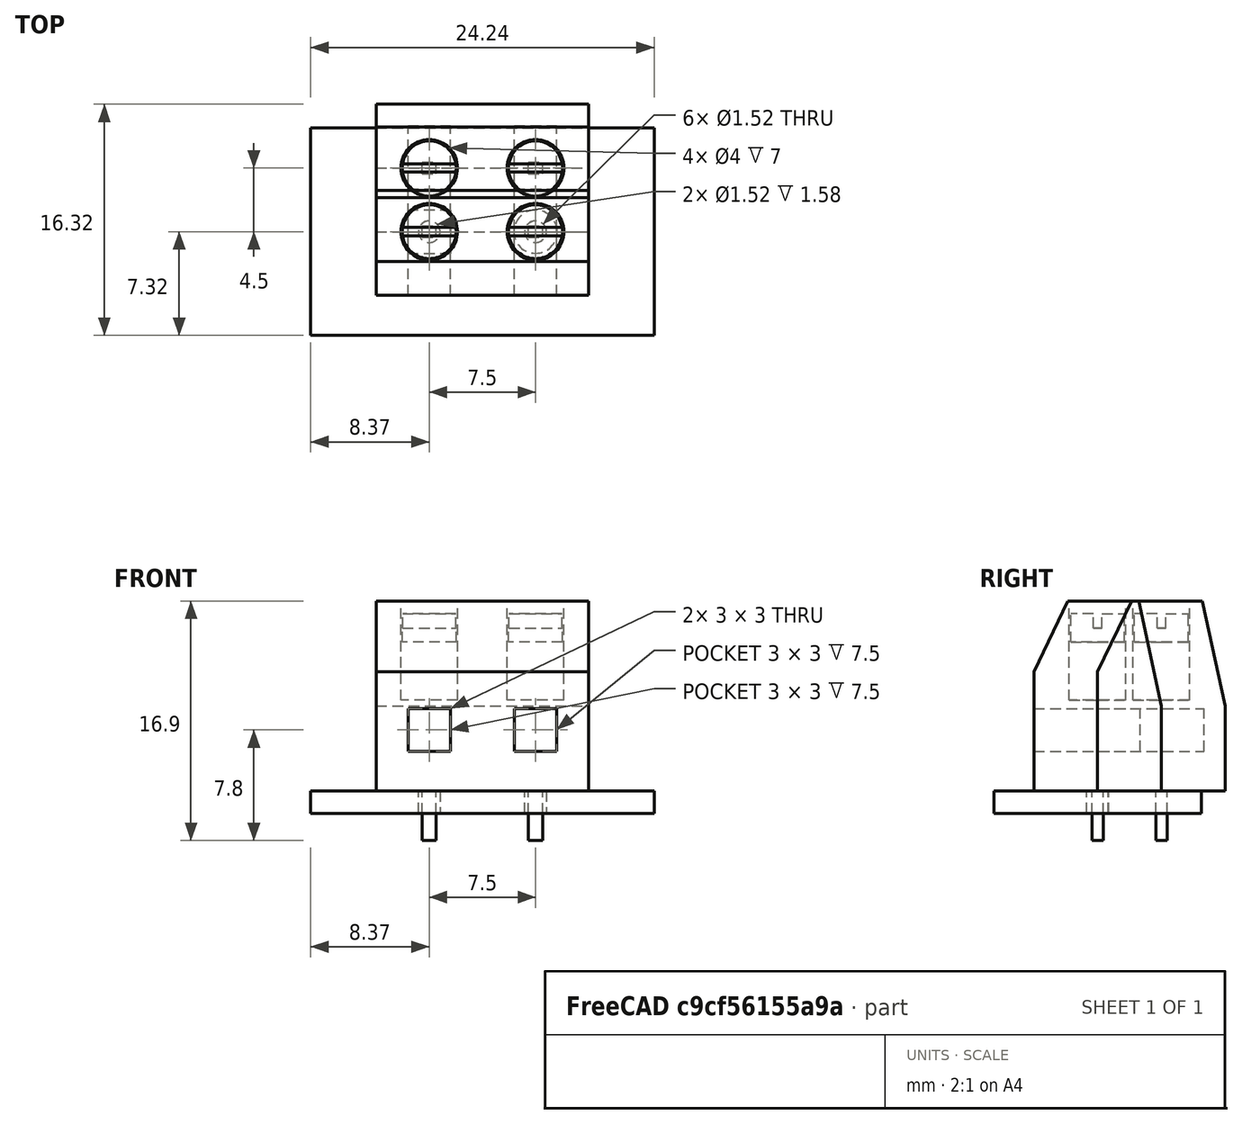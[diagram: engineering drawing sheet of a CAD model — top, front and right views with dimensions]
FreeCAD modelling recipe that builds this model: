
FCSTD DOCUMENT  (FreeCAD 0.18R16131 (Git))
Label: TerminalBlock_ED365-2_Angled_1x02_P7.50mm
License: All rights reserved
LicenseURL: http://en.wikipedia.org/wiki/All_rights_reserved
objects: Part::Box×6, Part::Cut×6, Part::FeaturePython×5, Part::Cylinder×4, Part::Part2DObjectPython×1, Part::Extrusion×1, App::DocumentObjectGroup×1, App::Part×1, Part::Feature×1
note: 24 computed .brp shape members not serialized (recipe doc carries the construction recipe); baked Part::Feature solids carry a one-line shape summary decoded from their .brp

FEATURE [Part::Part2DObjectPython] Wire  # Draft 2D object (typed FeaturePython)
  ChamferSize = 0
  Closed = true
  End = (0,0,0)
  FilletRadius = 0
  Length = 41.5172
  MakeFace = true
  Placement = pos=(0,0,0) rot=(0,0,-1;1.5708rad)
  Points = (7) [(0,0,0),(0,0,8.4),(-2.4,5.32907e-16,13.4),(-7.4,1.64313e-15,13.4),(-9,1.9984e-15,6),(-9,1.9984e-15,0),(0,0,0)]
  Start = (0,0,0)
  Subdivisions = 0
FEATURE [Part::Extrusion] Extrude
  Base = -> Wire
  Dir = (1,0,0)
  DirMode = 0
  FaceMakerClass = Part::FaceMakerBullseye
  LengthFwd = 7.5
  LengthRev = 7.5
  Solid = false
  Symmetric = false
FEATURE [Part::Box] Box  label="Pin 1"
  AttacherType = Attacher::AttachEngine3D
  Height = 3.5
  Length = 1
  Placement = pos=(-4.25,4.1,-3.5) rot=(0,0,1;0rad)
  Width = 0.8
FEATURE [Part::Box] Box001  label="Pin 2"
  AttacherType = Attacher::AttachEngine3D
  Height = 3.5
  Length = 1
  Placement = pos=(3.25,4.1,-3.5) rot=(0,0,1;0rad)
  Width = 0.8
FEATURE [Part::Box] Box002  label="Cube"
  AttacherType = Attacher::AttachEngine3D
  Height = 3
  Length = 3
  Placement = pos=(2.25,0,2.8) rot=(0,0,1;0rad)
  Width = 7.5
FEATURE [Part::Box] Box003  label="Cube001"
  AttacherType = Attacher::AttachEngine3D
  Height = 3
  Length = 3
  Placement = pos=(-5.25,0,2.8) rot=(0,0,1;0rad)
  Width = 7.5
FEATURE [Part::Cut] Cut
  Base = -> Extrude
  Tool = -> Box002
FEATURE [Part::Cut] Cut001
  Base = -> Cut
  Tool = -> Box003
FEATURE [Part::Cylinder] Cylinder001
  Angle = 360
  AttacherType = Attacher::AttachEngine3D
  Height = 7.1
  Placement = pos=(-3.75,4.5,6.4) rot=(0,0,1;0rad)
  Radius = 2
FEATURE [Part::Cut] Cut002
  Base = -> Cut001
  Tool = -> Cylinder001
FEATURE [Part::Cylinder] Cylinder002
  Angle = 360
  AttacherType = Attacher::AttachEngine3D
  Height = 2
  Radius = 1.9
FEATURE [Part::Box] Box004  label="Cube002"
  AttacherType = Attacher::AttachEngine3D
  Height = 1
  Length = 4
  Placement = pos=(-2,-0.3,1) rot=(0,0,1;0rad)
  Width = 0.6
FEATURE [Part::Cylinder] Cylinder
  Angle = 360
  AttacherType = Attacher::AttachEngine3D
  Height = 7.1
  Placement = pos=(3.75,4.5,6.4) rot=(0,0,1;0rad)
  Radius = 2
FEATURE [Part::Cut] Cut003  label="Plastic Body"
  Base = -> Cut002
  Tool = -> Cylinder
FEATURE [Part::Cut] Cut004  label="Screw 1"
  Base = -> Cylinder002
  Placement = pos=(-3.75,4.5,10.5) rot=(0,0,1;0rad)
  Tool = -> Box004
FEATURE [Part::Box] Box005  label="Cube003"
  AttacherType = Attacher::AttachEngine3D
  Height = 1
  Length = 4
  Placement = pos=(-2,-0.3,1) rot=(0,0,1;0rad)
  Width = 0.6
FEATURE [Part::Cylinder] Cylinder003
  Angle = 360
  AttacherType = Attacher::AttachEngine3D
  Height = 2
  Radius = 1.9
FEATURE [Part::Cut] Cut005  label="Screw 2"
  Base = -> Cylinder003
  Placement = pos=(3.75,4.5,10.5) rot=(0,0,1;0rad)
  Tool = -> Box005
FEATURE [Part::FeaturePython] Filk_lines  label="FrontSilk"  # a2plus imported part (geometry in sourceFile) (typed FeaturePython)
  fixedPosition = true
FEATURE [Part::FeaturePython] TopPads  # a2plus imported part (geometry in sourceFile) (typed FeaturePython)
  fixedPosition = true
FEATURE [Part::FeaturePython] BotPads  # a2plus imported part (geometry in sourceFile) (typed FeaturePython)
  fixedPosition = true
FEATURE [Part::FeaturePython] THPs  label="PTHs"  # a2plus imported part (geometry in sourceFile) (typed FeaturePython)
  fixedPosition = true
FEATURE [Part::FeaturePython] newPCB  label="Pcb"  # a2plus imported part (geometry in sourceFile) (typed FeaturePython)
  fixedPosition = true
FEATURE [App::DocumentObjectGroup] TerminalBlock_ED365_2_Angled_1x02_P7_50mm_fp
  Group = -> [Filk_lines,TopPads,BotPads,THPs,newPCB]
FEATURE [App::Part] Part  label="TerminalBlock_ED365-2_Angled_1x02_P7.50mm"
  Group = -> [Box,Box001,Box002,Box003,Cylinder,Cut001,Cut002,Cut,Wire,Cylinder001,Extrude,Cut003,Box004,Cylinder002,Cut004,Cylinder003,Box005,Cut005]
  Origin = -> Origin
FEATURE [Part::Feature] Shape001  label="TerminalBlock_ED365_2_Angled_1x02_P7_50mm_cp"
  shape: bbox 15 x 9 x 16.9 mm, 48 faces, 5 solids (baked)
